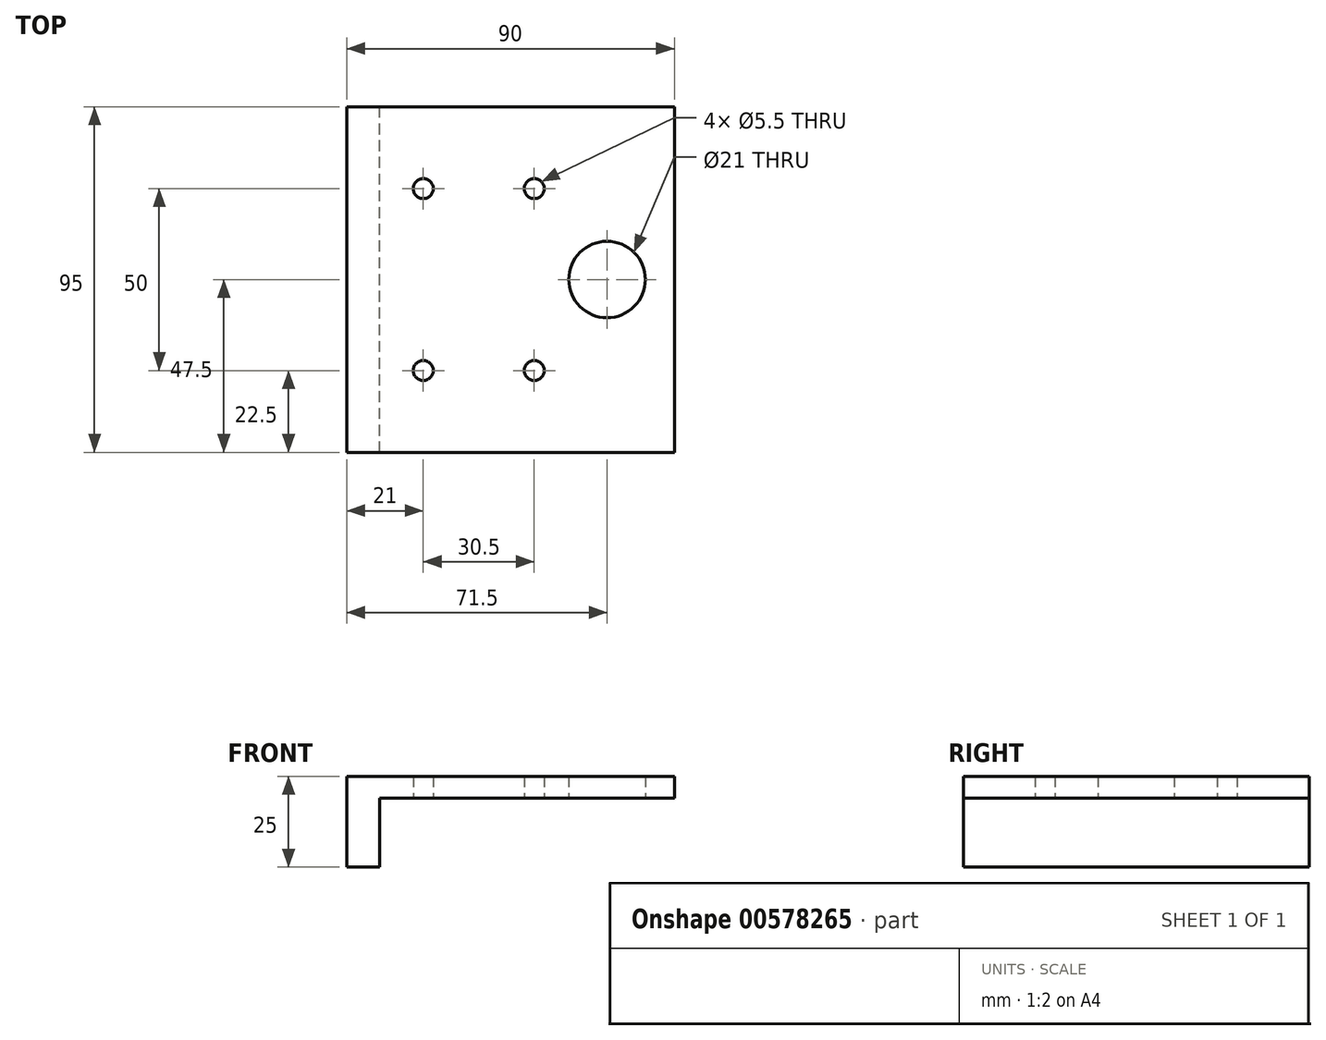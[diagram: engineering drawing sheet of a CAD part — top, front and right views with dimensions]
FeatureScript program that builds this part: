
annotation { "Feature Type Name" : "Feature", "Feature Type Description" : "" }
export const myFeature = defineFeature(function(context is Context, id is Id, definition is map)
    precondition{}
    {
        {
            var Q0;
            Q0=qCreatedBy(makeId("Front.planeOp"),FACE);
            var sketch = newSketch(context, id + "F0", { "sketchPlane" : qUnion([Q0])});
            skLineSegment(sketch, "E0", {"start": v(0, 0) * mm, "end": v(-90, 0) * mm});
            skLineSegment(sketch, "E1", {"start": v(-90, 0) * mm, "end": v(-90, -25) * mm});
            skLineSegment(sketch, "E2", {"start": v(-90, -25) * mm, "end": v(-81, -25) * mm});
            skLineSegment(sketch, "E3", {"start": v(-81, -25) * mm, "end": v(-81, -6) * mm});
            skLineSegment(sketch, "E4", {"start": v(-81, -6) * mm, "end": v(0, -6) * mm});
            skLineSegment(sketch, "E5", {"start": v(0, -6) * mm, "end": v(0, 0) * mm});
            skSolve(sketch);
        }
        {
            var Q0;
            Q0=qSketchRegion(id+"F0",true);
            extrude(context, id + "F1", {"entities" : qUnion([Q0]), "depth" : 95 * mm, "offsetDistance" : 25 * mm});
        }
        {
            var Q0;
            Q0=makeQuery(id+"F1.opExtrude","SWEPT_FACE",FACE,{"disambiguationData":[OSD([sQuery(id+"F0.wireOp",EDGE,"E4")])]});
            var sketch = newSketch(context, id + "F2", { "sketchPlane" : qUnion([Q0])});
            skCircle(sketch, "E6", {"center": v(-69, 72.5) * mm, "radius": 2.75 * mm});
            skCircle(sketch, "E7", {"center": v(-38.5, 72.5) * mm, "radius": 2.75 * mm});
            skCircle(sketch, "E8", {"center": v(-69, 22.5) * mm, "radius": 2.75 * mm});
            skCircle(sketch, "E9", {"center": v(-38.5, 22.5) * mm, "radius": 2.75 * mm});
            skCircle(sketch, "E10", {"center": v(-18.5, 47.5) * mm, "radius": 10.5 * mm});
            skSolve(sketch);
        }
        {
            var Q0;
            Q0=qSketchRegion(id+"F2",true);
            extrude(context, id + "F3", {"entities" : qUnion([Q0]), "operationType" : NewBodyOperationType.REMOVE, "oppositeDirection" : true, "depth" : 6 * mm, "offsetDistance" : 25 * mm});
        }
    });
